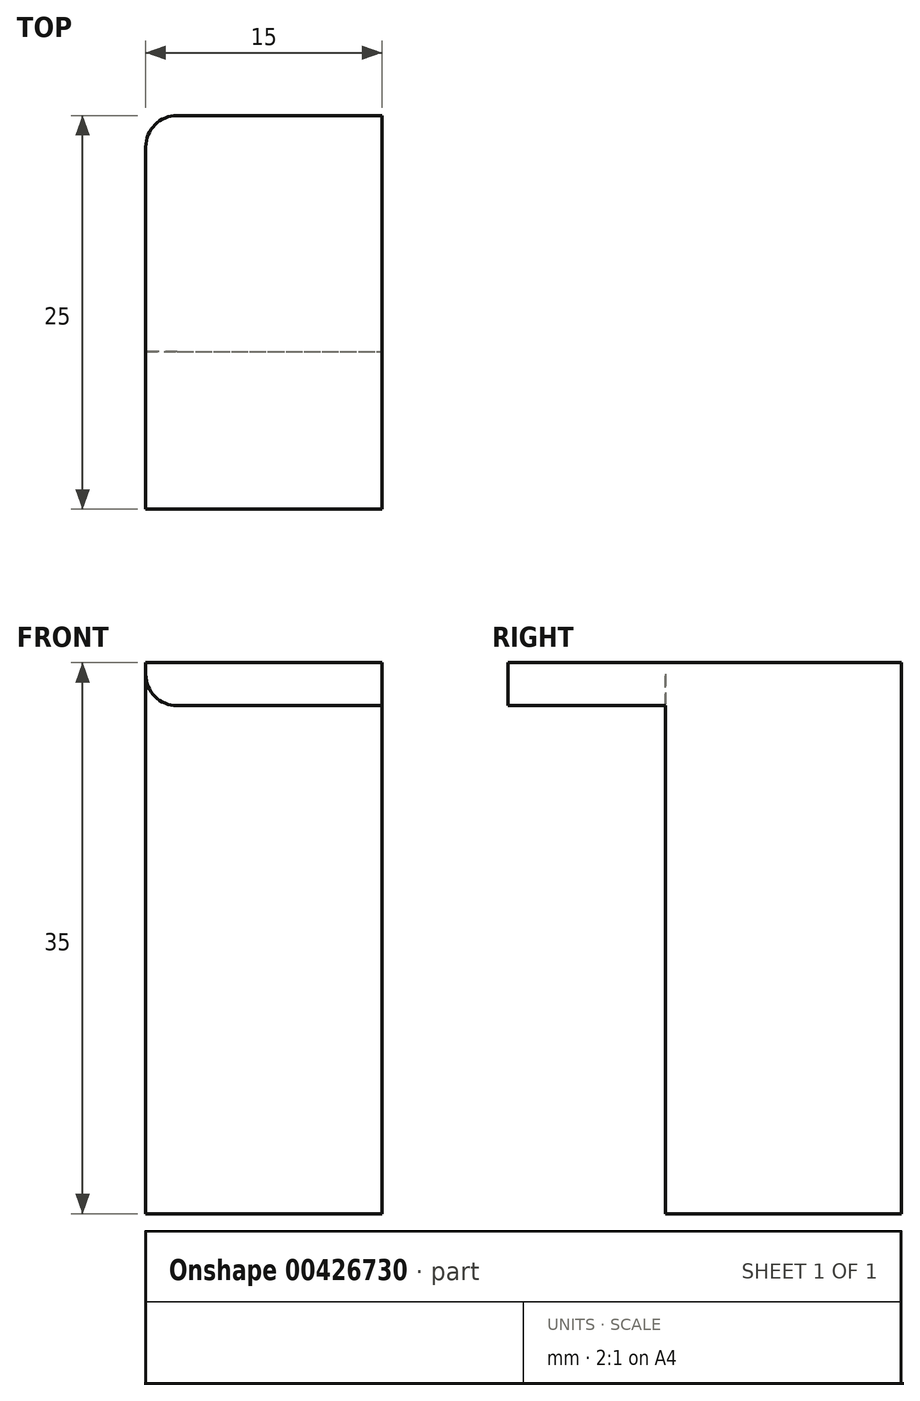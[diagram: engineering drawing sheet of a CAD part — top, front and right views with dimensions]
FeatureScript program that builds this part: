
annotation { "Feature Type Name" : "Feature", "Feature Type Description" : "" }
export const myFeature = defineFeature(function(context is Context, id is Id, definition is map)
    precondition{}
    {
        {
            var Q0;
            Q0=qCreatedBy(makeId("Top.planeOp"),FACE);
            var sketch = newSketch(context, id + "F0", { "sketchPlane" : qUnion([Q0])});
            skLineSegment(sketch, "E0.bottom", {"start": v(-5.69, 5.63) * mm, "end": v(9.31, 5.63) * mm});
            skLineSegment(sketch, "E0.top", {"start": v(-5.69, -9.37) * mm, "end": v(9.31, -9.37) * mm});
            skLineSegment(sketch, "E0.left", {"start": v(-5.69, 5.63) * mm, "end": v(-5.69, -9.37) * mm});
            skLineSegment(sketch, "E0.right", {"start": v(9.31, 5.63) * mm, "end": v(9.31, -9.37) * mm});
            skSolve(sketch);
        }
        {
            var Q0;
            Q0 = qSketchRegion(id + "F0", true);
            extrude(context, id + "F1", {"entities" : qUnion([Q0]), "depth" : 35 * mm});
        }
        {
            var Q0;
            Q0=makeQuery(id+"F1.opExtrude","SWEPT_FACE",FACE,{"disambiguationData":[OSD([sQuery(id+"F0.wireOp",EDGE,"E0.top")])]});
            var sketch = newSketch(context, id + "F2", { "sketchPlane" : qUnion([Q0])});
            skLineSegment(sketch, "E1.bottom", {"start": v(-5.69, 35) * mm, "end": v(9.31, 35) * mm});
            skLineSegment(sketch, "E1.top", {"start": v(-5.69, 32.26) * mm, "end": v(9.31, 32.26) * mm});
            skLineSegment(sketch, "E1.left", {"start": v(-5.69, 35) * mm, "end": v(-5.69, 32.26) * mm});
            skLineSegment(sketch, "E1.right", {"start": v(9.31, 35) * mm, "end": v(9.31, 32.26) * mm});
            skSolve(sketch);
        }
        {
            var Q0;
            Q0=makeQuery(id+"F2.imprint","IMPRINT",FACE,{"disambiguationData":[TD([[makeQuery(id+"F2.imprint","IMPRINT",EDGE,{"derivedFrom":sQuery(id+"F2.wireOp",EDGE,"E1.bottom")}),-1.0]])]});
            extrude(context, id + "F3", {"entities" : qUnion([Q0]), "operationType" : NewBodyOperationType.ADD, "depth" : 10 * mm});
        }
        {
            var Q0;
            Q0=makeQuery(id+"F1.opExtrude","SWEPT_EDGE",EDGE,{"disambiguationData":[OSD([sQuery(id+"F0.wireOp",EDGE,"E0.bottom"),sQuery(id+"F0.wireOp",EDGE,"E0.left")])]});
            fillet(context, id + "F4", {"entities" : qUnion([Q0]), "radius" : 2 * mm, "tangentPropagation" : true, "allowEdgeOverflow" : false});
        }
        {
            var Q0;
            Q0=makeQuery(id+"F3.opExtrude","SWEPT_EDGE",EDGE,{"disambiguationData":[OSD([sQuery(id+"F0.wireOp",EDGE,"E0.top"),sQuery(id+"F0.wireOp",EDGE,"E0.left"),sQuery(id+"F2.wireOp",EDGE,"E1.top"),sQuery(id+"F2.wireOp",EDGE,"E1.left")])]});
            fillet(context, id + "F5", {"entities" : qUnion([Q0]), "radius" : 2 * mm, "tangentPropagation" : true, "allowEdgeOverflow" : false});
        }
    });
